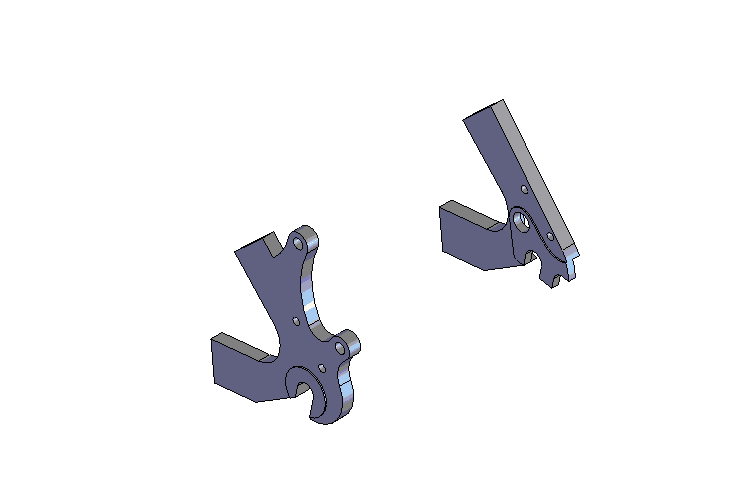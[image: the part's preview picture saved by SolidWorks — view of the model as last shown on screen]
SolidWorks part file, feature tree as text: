
SOLIDWORKS PART (.sldprt)
format: sldprt  version: not decoded by parser v0  size: 699,904 bytes
history: native  units: mm
features: sketch x8, plane x5, extrude x4, cut_extrude x3, material x1 (+10 scaffold rows collapsed)
feature tree (31):
  scaffold x10  (default folders/planes/origin — collapsed)
  material  "Matériau <non spécifié>"
  plane  "Plan de face"
  plane  "Plan de dessus"
  plane  "Plan de droite"
  sketch  "Esquisse1"  dims[c1.D13=30.0mm c1.D14=14.0mm c1.D1=625.0mm c1.D2=460.0mm c1.D3=545.0mm c1.D4=27.0mm c1.D5=500.0mm c1.D6=445.0mm c1.D7=670.0mm c2.D1=622.0mm c2.D2=670.0mm c2.D3=545.0mm c2.D4=460.0mm c2.D5=445.0mm c2.D6=495.0mm c2.D7=535.0mm c2.D8=27.0mm c2.D9=8.0mm c2.D10=155.0mm c2.D11=400.0mm c2.D12=~545.374305mm c3.D12=56.0deg]
  plane  "Plan1"  Offset=71.75mm
  sketch  "Esquisse24"  dims[c1.D1=10.0mm c1.D2=15.0mm c1.D3=19.0mm c1.D5=6.0mm c1.D6=6.0mm c1.D8=~13.175347mm c1.D15=12.0mm c1.D18=6.0mm c1.D19=16.0mm c1.D20=44.0mm c2.D6=8.0mm c2.D19=8.0mm c2.D22=19.0mm c3.D19=13.0mm c3.D23=8.0mm c3.D24=30.0mm c3.D1=~23.333356mm c3.D4=460.0mm c4.D4=~76.317285deg c5.D4=~104.669232mm c6.D4=~118.797025deg c7.D4=460.0mm c8.D4=72.0deg c8.D7=40.0mm c8.D8=23.0mm c8.D9=30.0mm c8.D10=60.0mm c8.D11=7.0mm c8.D12=13.0mm c8.D13=24.0mm c8.D14=70.0mm c8.D16=78.0mm c8.D17=78.0mm c8.D18=78.0mm c9.D17=78.0mm c9.D16=78.0mm c10.D17=34.0mm c10.D21=10.0mm c10.D18=51.0mm c10.D19=12.0mm c10.D22=20.0mm c10.D23=20.0mm c11.D22=20.0mm c11.D23=12.0mm c12.D22=20.0mm c12.D23=20.0mm c13.D22=20.0mm c13.D23=20.0mm c14.D22=20.0mm c14.D23=20.0mm c15.D22=20.0mm c15.D23=20.0mm c15.D19=12.0mm c16.D22=21.5mm c16.D23=28.0mm]
  extrude  "Extrusion8"  Depth=7mm
  sketch  "Esquisse25"  dims[D1=6.0mm D2=4.2mm D3=20.0mm D4=35.0mm D5=4.0mm]
  cut_extrude  "Enlèv. mat.-Extru.7"  [1 undecoded]
  sketch  "Esquisse26"  dims[D1=25.0mm]
  extrude  "Extrusion9"  Depth=8.5mm
  plane  "Plan2"  Offset=143.5mm
  sketch  "Esquisse27"  dims[c1.D1=44.0mm c1.D3=5.0mm c2.D1=22.0mm c2.D2=8.0mm c2.D4=11.0mm]
  extrude  "Extrusion10"  Depth=3.5mm
  sketch  "Esquisse31"  dims[c1.D1=2.0mm c1.D4=7.5mm c1.D5=2.0mm c1.D6=~13.241643mm c1.D7=13.5mm c1.D8=5.0mm c1.D2=11.0mm c1.D3=15.0mm c2.D5=~18.585558mm c2.D1=24.0mm c2.D6=19.5mm c2.D8=8.5mm c2.D9=~11.629052mm c3.D9=~147.740764deg]
  cut_extrude  "Enlèv. mat.-Extru.8"  [1 undecoded]
  sketch  "Esquisse32"  dims[D1=0.0mm]
  extrude  "Extrusion11"  Depth=4.25mm
  sketch  "Esquisse29"  dims[D1=10.0mm]
  cut_extrude  "Enlèv. mat.-Extru.9"  [1 undecoded]
decode coverage: 12 of 15 modeling features carry decoded parameters
note: ~ marks probable driven/reference dimensions
note: 3 parameter values undecoded
summary: no parameter record found for 3 features
note: suppression state not decoded; provenance and decode notes live in map.json
